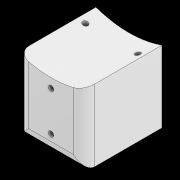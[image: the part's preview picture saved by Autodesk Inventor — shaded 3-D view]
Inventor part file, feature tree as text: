
AUTODESK INVENTOR PART (.ipt)
format: ipt  version: 2022.2 (Build 262287010, 287A)  size: 344,576 bytes
history: native  units: mm
features: extrude x14, sketch x13, other x3, pattern_circular x3, fillet x2, plane x1, hole x1
ambient origin geometry x8: Origin, YZ Plane, XZ Plane, XY Plane, X Axis, Y Axis, Z Axis, Center Point
bodies: Solid3 (feature_tree)
feature tree (37):
  other  "CrossSection1"
  sketch  "Sketch3"  dims[d59=66.75mm d61=0.0mm d62=3600.0mm]
  sketch  "Sketch1"  dims[d4=150.0mm d19=12.0mm]
  plane  "Work Plane1"
  sketch  "Sketch9"  dims[d91=23.65mm]
  extrude  "Extrusion7"  Depth=12.0mm
  sketch  "Sketch10"  dims[d97=26.0mm d98=0.0mm]
  extrude  "Extrusion10"  Depth=3600.0mm TaperAngle=0.0deg
  pattern_circular  "Circular Pattern4"  Count=360  [1 undecoded]
  extrude  "Extrusion8"  Depth=69.0mm
  extrude  "Extrusion9"  Depth=8.0mm
  pattern_circular  "Circular Pattern3"  [2 undecoded]
  extrude  "Extrusion3"  Depth=8.0mm
  hole  "Hole3"  [1 undecoded]
  pattern_circular  "Circular Pattern5"  Count=5 Angle=360.0deg
  sketch  "Sketch13"  dims[d104=2.0mm d105=0.0mm d106=3600.0mm]
  extrude  "Extrusion12"  Depth=8.0mm TaperAngle=0.0deg
  extrude  "Extrusion13"  Depth=8.0mm TaperAngle=360.0deg
  extrude  "Extrusion14"  Depth=8.0mm
  sketch  "Sketch14"  dims[d111=100.0mm d112=69.0mm]
  extrude  "Extrusion15"  Depth=8.0mm TaperAngle=0.0deg
  extrude  "Extrusion16"  Depth=8.0mm
  extrude  "Extrusion17"  Depth=8.0mm TaperAngle=360.0deg
  fillet  "Fillet2"  Radius=0.5mm
  sketch  "Sketch4"  dims[d66=12.0mm]
  sketch  "Sketch5"  dims[d67=63.483mm]
  extrude  "Extrusion4"  Depth=8.0mm
  sketch  "Sketch7"  dims[d68=138.0mm]
  extrude  "Extrusion6"  Depth=8.0mm
  fillet  "Fillet1"  Radius=7.0mm
  extrude  "Extrusion11"  Depth=8.0mm
  other  "2D Equation Curve10"
  sketch  "Sketch8"  dims[d69=26.3mm d70=0.0mm]
  other  "2D Equation Curve11"
  sketch  "Sketch11"  dims[d99=156.0mm]
  sketch  "Sketch12"  dims[d102=29.0mm d103=0.0mm]
  sketch  "Sketch15"  dims[d113=2.5mm d114=0.0mm d115=3.0mm d116=0.0mm d117=0.0mm d118=5.5mm d119=2.5mm d120=0.0mm d121=50.0mm d122=360.0deg d124=2.5mm d125=0.0mm d126=50.0mm d127=360.0deg d129=22.5mm d130=2.5mm d131=0.0mm d132=138.0mm d133=4.0mm d134=6.0mm d135=4.0mm d136=2.0mm d137=90.0deg d138=4.0mm d139=0.0mm d140=50.0mm d141=360.0deg d143=0.5mm d144=2.0mm d145=0.0mm d146=20.0mm d147=3.1416mm d148=3.141586mm d149=7.0mm d150=7.0mm d151=65.564mm d152=0.0mm d153=4.0mm d154=4.0mm d155=0.0mm d156=0.0mm d157=82.0mm d158=30.0mm d159=4.0mm d160=4.0mm d161=25.0mm d162=25.0mm d163=25.0mm d164=25.0mm d165=50.0mm d168=26.3mm d169=0.0mm d170=26.3mm d171=0.0mm d172=4.0mm d173=0.0mm d174=32.694mm d175=0.0mm d176=8.0mm]
note: 4 required parameter values undecoded (feature->parameter linkage not recoverable at this tier; creation-order binding heuristic only, values carry confidence <= 0.55)
